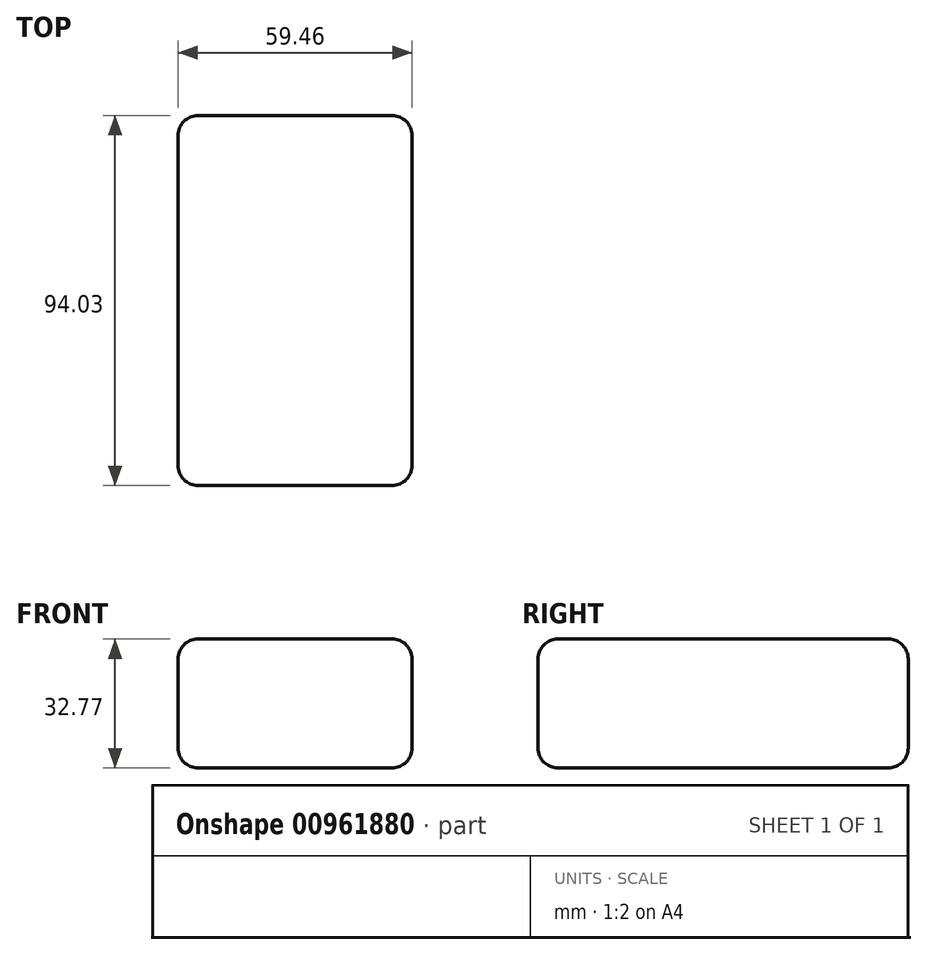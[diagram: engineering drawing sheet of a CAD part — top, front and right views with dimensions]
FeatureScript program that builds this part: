
annotation { "Feature Type Name" : "Feature", "Feature Type Description" : "" }
export const myFeature = defineFeature(function(context is Context, id is Id, definition is map)
    precondition{}
    {
        {
            var Q0;
            Q0=qCreatedBy(makeId("Top.planeOp"),FACE);
            var sketch = newSketch(context, id + "F0", { "sketchPlane" : qUnion([Q0])});
            skLineSegment(sketch, "E0.bottom", {"start": v(-50.92, 55.48) * mm, "end": v(8.54, 55.48) * mm});
            skLineSegment(sketch, "E0.top", {"start": v(-50.92, -38.55) * mm, "end": v(8.54, -38.55) * mm});
            skLineSegment(sketch, "E0.left", {"start": v(-50.92, 55.48) * mm, "end": v(-50.92, -38.55) * mm});
            skLineSegment(sketch, "E0.right", {"start": v(8.54, 55.48) * mm, "end": v(8.54, -38.55) * mm});
            skSolve(sketch);
        }
        {
            var Q0;
            Q0=makeQuery(id+"F0.imprint","IMPRINT",FACE,{"disambiguationData":[TD([[makeQuery(id+"F0.imprint","IMPRINT",EDGE,{"derivedFrom":sQuery(id+"F0.wireOp",EDGE,"E0.bottom")}),-1.0]])]});
            extrude(context, id + "F1", {"entities" : qUnion([Q0]), "depth" : 32.77 * mm, "offsetDistance" : 25.4 * mm});
        }
        {
            var Q0;
            Q0=makeQuery(id+"F1.opExtrude","CAP_EDGE",EDGE,{"disambiguationData":[OSD([sQuery(id+"F0.wireOp",EDGE,"E0.right")])],"isStart":false});
            var Q1;
            Q1=makeQuery(id+"F1.opExtrude","SWEPT_EDGE",EDGE,{"disambiguationData":[OSD([sQuery(id+"F0.wireOp",EDGE,"E0.top"),sQuery(id+"F0.wireOp",EDGE,"E0.right")])]});
            var Q2;
            Q2=makeQuery(id+"F1.opExtrude","CAP_EDGE",EDGE,{"disambiguationData":[OSD([sQuery(id+"F0.wireOp",EDGE,"E0.right")])],"isStart":true});
            var Q3;
            Q3=makeQuery(id+"F1.opExtrude","SWEPT_EDGE",EDGE,{"disambiguationData":[OSD([sQuery(id+"F0.wireOp",EDGE,"E0.bottom"),sQuery(id+"F0.wireOp",EDGE,"E0.right")])]});
            var Q4;
            Q4=makeQuery(id+"F1.opExtrude","CAP_EDGE",EDGE,{"disambiguationData":[OSD([sQuery(id+"F0.wireOp",EDGE,"E0.top")])],"isStart":false});
            var Q5;
            Q5=makeQuery(id+"F1.opExtrude","CAP_EDGE",EDGE,{"disambiguationData":[OSD([sQuery(id+"F0.wireOp",EDGE,"E0.top")])],"isStart":true});
            var Q6;
            Q6=makeQuery(id+"F1.opExtrude","SWEPT_EDGE",EDGE,{"disambiguationData":[OSD([sQuery(id+"F0.wireOp",EDGE,"E0.top"),sQuery(id+"F0.wireOp",EDGE,"E0.left")])]});
            var Q7;
            Q7=makeQuery(id+"F1.opExtrude","CAP_EDGE",EDGE,{"disambiguationData":[OSD([sQuery(id+"F0.wireOp",EDGE,"E0.left")])],"isStart":false});
            var Q8;
            Q8=makeQuery(id+"F1.opExtrude","CAP_EDGE",EDGE,{"disambiguationData":[OSD([sQuery(id+"F0.wireOp",EDGE,"E0.bottom")])],"isStart":false});
            var Q9;
            Q9=makeQuery(id+"F1.opExtrude","CAP_EDGE",EDGE,{"disambiguationData":[OSD([sQuery(id+"F0.wireOp",EDGE,"E0.left")])],"isStart":true});
            var Q10;
            Q10=makeQuery(id+"F1.opExtrude","SWEPT_EDGE",EDGE,{"disambiguationData":[OSD([sQuery(id+"F0.wireOp",EDGE,"E0.bottom"),sQuery(id+"F0.wireOp",EDGE,"E0.left")])]});
            var Q11;
            Q11=makeQuery(id+"F1.opExtrude","CAP_EDGE",EDGE,{"disambiguationData":[OSD([sQuery(id+"F0.wireOp",EDGE,"E0.bottom")])],"isStart":true});
            fillet(context, id + "F2", {"entities" : qUnion([Q0, Q1, Q2, Q3, Q4, Q5, Q6, Q7, Q8, Q9, Q10, Q11]), "radius" : 5.08 * mm, "tangentPropagation" : true, "allowEdgeOverflow" : false});
        }
    });
